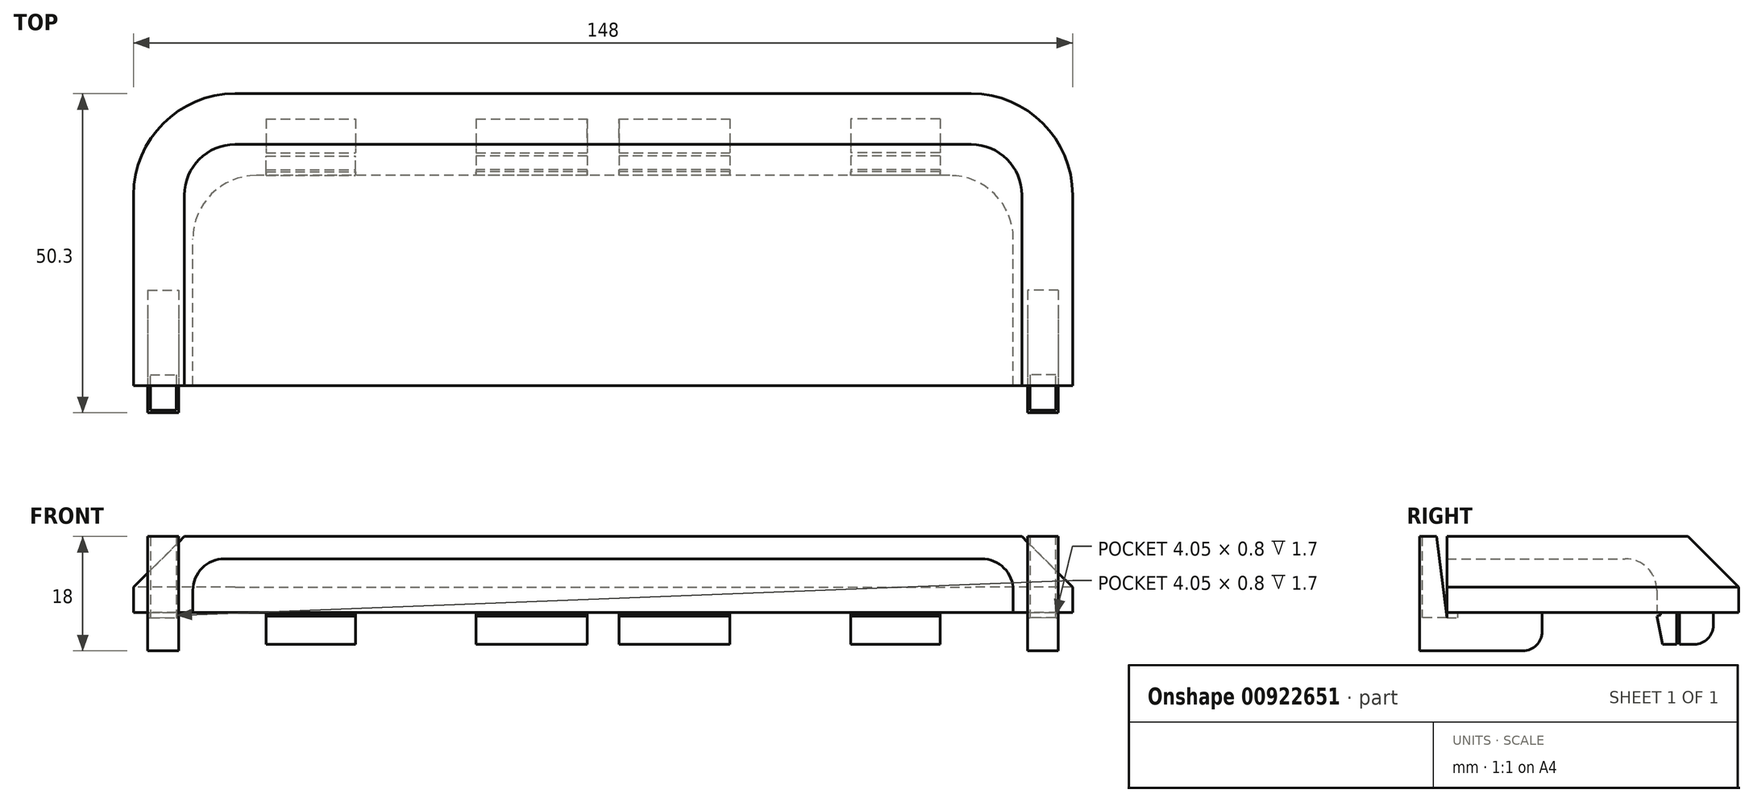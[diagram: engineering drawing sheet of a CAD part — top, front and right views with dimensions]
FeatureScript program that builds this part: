
annotation { "Feature Type Name" : "Feature", "Feature Type Description" : "" }
export const myFeature = defineFeature(function(context is Context, id is Id, definition is map)
    precondition{}
    {
        {
            var Q0;
            Q0=qCreatedBy(makeId("Top.planeOp"),FACE);
            var sketch = newSketch(context, id + "F0", { "sketchPlane" : qUnion([Q0])});
            skLineSegment(sketch, "E0.bottom", {"start": v(-20, 0) * mm, "end": v(20, 0) * mm});
            skLineSegment(sketch, "E0.top", {"start": v(-20, -8.3) * mm, "end": v(20, -8.3) * mm});
            skLineSegment(sketch, "E0.left", {"start": v(-20, 0) * mm, "end": v(-20, -8.3) * mm});
            skLineSegment(sketch, "E0.right", {"start": v(20, 0) * mm, "end": v(20, -8.3) * mm});
            skLineSegment(sketch, "E1.bottom", {"start": v(-53.1, 0) * mm, "end": v(-39, 0) * mm});
            skLineSegment(sketch, "E1.top", {"start": v(-53.1, -8.3) * mm, "end": v(-39, -8.3) * mm});
            skLineSegment(sketch, "E1.left", {"start": v(-53.1, 0) * mm, "end": v(-53.1, -8.3) * mm});
            skLineSegment(sketch, "E1.right", {"start": v(-39, 0) * mm, "end": v(-39, -8.3) * mm});
            skLineSegment(sketch, "E2.MirrorCS", {"start": v(53.1, -8.3) * mm, "end": v(39, -8.3) * mm});
            skLineSegment(sketch, "E3.MirrorCS", {"start": v(39, 0) * mm, "end": v(39, -8.3) * mm});
            skLineSegment(sketch, "E4.MirrorCS", {"start": v(53.1, 0) * mm, "end": v(39, 0) * mm});
            skLineSegment(sketch, "E5.MirrorCS", {"start": v(53.1, 0) * mm, "end": v(53.1, -8.3) * mm});
            skLineSegment(sketch, "E6.bottom", {"start": v(-71.75, -27) * mm, "end": v(-66.9, -27) * mm});
            skLineSegment(sketch, "E6.top", {"start": v(-71.75, -40.3) * mm, "end": v(-66.9, -40.3) * mm});
            skLineSegment(sketch, "E6.left", {"start": v(-71.75, -27) * mm, "end": v(-71.75, -40.3) * mm});
            skLineSegment(sketch, "E6.right", {"start": v(-66.9, -27) * mm, "end": v(-66.9, -40.3) * mm});
            skLineSegment(sketch, "E7.MirrorCS", {"start": v(71.75, -27) * mm, "end": v(66.9, -27) * mm});
            skLineSegment(sketch, "E8.MirrorCS", {"start": v(71.75, -27) * mm, "end": v(71.75, -40.3) * mm});
            skLineSegment(sketch, "E9.MirrorCS", {"start": v(71.75, -40.3) * mm, "end": v(66.9, -40.3) * mm});
            skLineSegment(sketch, "E10.MirrorCS", {"start": v(66.9, -27) * mm, "end": v(66.9, -40.3) * mm});
            skLineSegment(sketch, "E11.bottom", {"start": v(-75, 10.7) * mm, "end": v(75, 10.7) * mm});
            skLineSegment(sketch, "E11.top", {"start": v(-75, -54.3) * mm, "end": v(75, -54.3) * mm});
            skLineSegment(sketch, "E11.left", {"start": v(-75, 10.7) * mm, "end": v(-75, -54.3) * mm});
            skLineSegment(sketch, "E11.right", {"start": v(75, 10.7) * mm, "end": v(75, -54.3) * mm});
            skSolve(sketch);
        }
        {
            var Q0;
            Q0=qCreatedBy(makeId("Top.planeOp"),FACE);
            var sketch = newSketch(context, id + "F1", { "sketchPlane" : qUnion([Q0])});
            skLineSegment(sketch, "E12.bottom", {"start": v(-58, 4) * mm, "end": v(58, 4) * mm});
            skLineSegment(sketch, "E12.top", {"start": v(-74, -42) * mm, "end": v(74, -42) * mm});
            skLineSegment(sketch, "E12.left", {"start": v(-74, -12) * mm, "end": v(-74, -42) * mm});
            skLineSegment(sketch, "E12.right", {"start": v(74, -12) * mm, "end": v(74, -42) * mm});
            skPoint(sketch, "E13.visualSharp", {"position": v(74, 4) * mm});
            skArc(sketch, "E13.filletArc", {"start": v(74, -12) * mm, "mid": v(69.31, -0.69) * mm, "end": v(58, 4) * mm});
            skPoint(sketch, "E14.visualSharp", {"position": v(-74, 4) * mm});
            skArc(sketch, "E14.filletArc", {"start": v(-58, 4) * mm, "mid": v(-69.31, -0.69) * mm, "end": v(-74, -12) * mm});
            skSolve(sketch);
        }
        {
            var Q0;
            Q0 = qSketchRegion(id + "F1", true);
            extrude(context, id + "F2", {"entities" : qUnion([Q0]), "depth" : 12 * mm, "offsetDistance" : 25 * mm});
        }
        {
            var Q0;
            Q0=makeQuery(id+"F2.opExtrude","CAP_EDGE",EDGE,{"disambiguationData":[OSD([sQuery(id+"F1.wireOp",EDGE,"E12.right")])],"isStart":false});
            var Q1;
            Q1=makeQuery(id+"F2.opExtrude","CAP_EDGE",EDGE,{"disambiguationData":[OSD([sQuery(id+"F1.wireOp",EDGE,"E12.bottom")])],"isStart":false});
            var Q2;
            Q2=makeQuery(id+"F2.opExtrude","CAP_EDGE",EDGE,{"disambiguationData":[OSD([sQuery(id+"F1.wireOp",EDGE,"E12.left")])],"isStart":false});
            chamfer(context, id + "F3", {"entities" : qUnion([Q0, Q1, Q2]), "width" : 8 * mm, "tangentPropagation" : true});
        }
        {
            var Q0;
            Q0=makeQuery(id+"F0.imprint","IMPRINT",FACE,{"disambiguationData":[TD([[makeQuery(id+"F0.imprint","IMPRINT",EDGE,{"derivedFrom":sQuery(id+"F0.wireOp",EDGE,"E1.bottom")}),-1.0]])]});
            var Q1;
            Q1=makeQuery(id+"F0.imprint","IMPRINT",FACE,{"disambiguationData":[TD([[makeQuery(id+"F0.imprint","IMPRINT",EDGE,{"derivedFrom":sQuery(id+"F0.wireOp",EDGE,"E0.bottom")}),-1.0]])]});
            var Q2;
            Q2=makeQuery(id+"F0.imprint","IMPRINT",FACE,{"disambiguationData":[TD([[makeQuery(id+"F0.imprint","IMPRINT",EDGE,{"derivedFrom":sQuery(id+"F0.wireOp",EDGE,"E2.MirrorCS")}),-1.0]])]});
            extrude(context, id + "F4", {"entities" : qUnion([Q0, Q1, Q2]), "operationType" : NewBodyOperationType.ADD, "oppositeDirection" : true, "depth" : 5 * mm, "offsetDistance" : 25 * mm});
        }
        {
            var Q0;
            Q0=qCreatedBy(makeId("Right.planeOp"),FACE);
            var sketch = newSketch(context, id + "F5", { "sketchPlane" : qUnion([Q0])});
            skLineSegment(sketch, "E15", {"start": v(-8.3, 0) * mm, "end": v(-8.3, -0.35) * mm});
            skLineSegment(sketch, "E16", {"start": v(-8.3, -0.35) * mm, "end": v(-8.9, -0.55) * mm});
            skLineSegment(sketch, "E17", {"start": v(-8.9, -0.55) * mm, "end": v(-8, -5) * mm});
            skLineSegment(sketch, "E18", {"start": v(-8, -5) * mm, "end": v(-5.8, -5) * mm});
            skLineSegment(sketch, "E19", {"start": v(-5.8, -5) * mm, "end": v(-5.8, 0) * mm});
            skLineSegment(sketch, "E20", {"start": v(-8.3, 0) * mm, "end": v(-5.8, 0) * mm});
            skSolve(sketch);
        }
        {
            var Q0;
            Q0=makeQuery(id+"F4.opExtrude","SWEPT_FACE",FACE,{"disambiguationData":[OSD([sQuery(id+"F0.wireOp",EDGE,"E0.top")])]});
            var Q1;
            Q1=makeQuery(id+"F4.opExtrude","SWEPT_FACE",FACE,{"disambiguationData":[OSD([sQuery(id+"F0.wireOp",EDGE,"E2.MirrorCS")])]});
            var Q2;
            Q2=makeQuery(id+"F4.opExtrude","SWEPT_FACE",FACE,{"disambiguationData":[OSD([sQuery(id+"F0.wireOp",EDGE,"E1.top")])]});
            extrude(context, id + "F6", {"entities" : qUnion([Q0, Q1, Q2]), "operationType" : NewBodyOperationType.REMOVE, "oppositeDirection" : true, "depth" : 3 * mm, "offsetDistance" : 25 * mm});
        }
        {
            var Q0;
            Q0 = qSketchRegion(id + "F5", true);
            var Q1;
            Q1=makeQuery(id+"F4.opExtrude","SWEPT_FACE",FACE,{"disambiguationData":[OSD([sQuery(id+"F0.wireOp",EDGE,"E0.right")])]});
            var Q2;
            Q2=makeQuery(id+"F4.opExtrude","SWEPT_FACE",FACE,{"disambiguationData":[OSD([sQuery(id+"F0.wireOp",EDGE,"E0.left")])]});
            extrude(context, id + "F7", {"entities" : qUnion([Q0]), "operationType" : NewBodyOperationType.ADD, "endBound" : BoundingType.UP_TO_SURFACE, "depth" : 25 * mm, "endBoundEntityFace" : qUnion([Q1]), "offsetDistance" : 25 * mm, "hasSecondDirection" : true, "secondDirectionBound" : BoundingType.UP_TO_SURFACE, "secondDirectionOppositeDirection" : true, "secondDirectionDepth" : 25 * mm, "secondDirectionBoundEntityFace" : qUnion([Q2])});
        }
        {
            var Q0;
            Q0 = qSketchRegion(id + "F5", true);
            var Q1;
            Q1=makeQuery(id+"F4.opExtrude","SWEPT_FACE",FACE,{"disambiguationData":[OSD([sQuery(id+"F0.wireOp",EDGE,"E5.MirrorCS")])]});
            var Q2;
            Q2=makeQuery(id+"F4.opExtrude","SWEPT_FACE",FACE,{"disambiguationData":[OSD([sQuery(id+"F0.wireOp",EDGE,"E3.MirrorCS")])]});
            extrude(context, id + "F8", {"entities" : qUnion([Q0]), "operationType" : NewBodyOperationType.ADD, "endBound" : BoundingType.UP_TO_SURFACE, "depth" : 25 * mm, "endBoundEntityFace" : qUnion([Q1]), "offsetDistance" : 25 * mm, "hasSecondDirection" : true, "secondDirectionBound" : BoundingType.UP_TO_SURFACE, "secondDirectionOppositeDirection" : false, "secondDirectionDepth" : 25 * mm, "secondDirectionBoundEntityFace" : qUnion([Q2])});
        }
        {
            var Q0;
            Q0 = qSketchRegion(id + "F5", true);
            var Q1;
            Q1=makeQuery(id+"F4.opExtrude","SWEPT_FACE",FACE,{"disambiguationData":[OSD([sQuery(id+"F0.wireOp",EDGE,"E1.left")])]});
            var Q2;
            Q2=makeQuery(id+"F4.opExtrude","SWEPT_FACE",FACE,{"disambiguationData":[OSD([sQuery(id+"F0.wireOp",EDGE,"E1.right")])]});
            extrude(context, id + "F9", {"entities" : qUnion([Q0]), "operationType" : NewBodyOperationType.ADD, "endBound" : BoundingType.UP_TO_SURFACE, "oppositeDirection" : true, "depth" : 25 * mm, "endBoundEntityFace" : qUnion([Q1]), "offsetDistance" : 25 * mm, "hasSecondDirection" : true, "secondDirectionBound" : BoundingType.UP_TO_SURFACE, "secondDirectionOppositeDirection" : true, "secondDirectionDepth" : 25 * mm, "secondDirectionBoundEntityFace" : qUnion([Q2])});
        }
        {
            var Q0;
            Q0=makeQuery(id+"F0.imprint","IMPRINT",FACE,{"disambiguationData":[TD([[makeQuery(id+"F0.imprint","IMPRINT",EDGE,{"derivedFrom":sQuery(id+"F0.wireOp",EDGE,"E7.MirrorCS")}),1.0]])]});
            var Q1;
            Q1=makeQuery(id+"F0.imprint","IMPRINT",FACE,{"disambiguationData":[TD([[makeQuery(id+"F0.imprint","IMPRINT",EDGE,{"derivedFrom":sQuery(id+"F0.wireOp",EDGE,"E6.bottom")}),-1.0]])]});
            extrude(context, id + "F10", {"entities" : qUnion([Q0, Q1]), "operationType" : NewBodyOperationType.ADD, "oppositeDirection" : true, "depth" : 6 * mm, "offsetDistance" : 25 * mm});
        }
        {
            var Q0;
            Q0=makeQuery(id+"F2.opExtrude","CAP_FACE",FACE,{"disambiguationData":[OSD([sQuery(id+"F1.wireOp",EDGE,"E12.bottom"),sQuery(id+"F1.wireOp",EDGE,"E12.top"),sQuery(id+"F1.wireOp",EDGE,"E12.left"),sQuery(id+"F1.wireOp",EDGE,"E12.right"),sQuery(id+"F1.wireOp",EDGE,"E13.filletArc"),sQuery(id+"F1.wireOp",EDGE,"E14.filletArc")])],"isStart":true});
            var sketch = newSketch(context, id + "F11", { "sketchPlane" : qUnion([Q0])});
            skLineSegment(sketch, "E21.bottom", {"start": v(64.65, 42) * mm, "end": v(-64.65, 42) * mm});
            skLineSegment(sketch, "E21.top", {"start": v(54.65, 8.9) * mm, "end": v(-54.65, 8.9) * mm});
            skLineSegment(sketch, "E21.left", {"start": v(64.65, 42) * mm, "end": v(64.65, 18.9) * mm});
            skLineSegment(sketch, "E21.right", {"start": v(-64.65, 42) * mm, "end": v(-64.65, 18.9) * mm});
            skLineSegment(sketch, "E22.0", {"start": v(66, 42) * mm, "end": v(66, 12) * mm, "construction": true});
            skLineSegment(sketch, "E23.0", {"start": v(58, 4) * mm, "end": v(-58, 4) * mm, "construction": true});
            skPoint(sketch, "E24.visualSharp", {"position": v(64.65, 8.9) * mm});
            skArc(sketch, "E24.filletArc", {"start": v(54.65, 8.9) * mm, "mid": v(61.72, 11.83) * mm, "end": v(64.65, 18.9) * mm});
            skPoint(sketch, "E25.visualSharp", {"position": v(-64.65, 8.9) * mm});
            skArc(sketch, "E25.filletArc", {"start": v(-64.65, 18.9) * mm, "mid": v(-61.72, 11.83) * mm, "end": v(-54.65, 8.9) * mm});
            skSolve(sketch);
        }
        {
            var Q0;
            Q0 = qSketchRegion(id + "F11", true);
            extrude(context, id + "F12", {"entities" : qUnion([Q0]), "operationType" : NewBodyOperationType.REMOVE, "oppositeDirection" : true, "depth" : 8.5 * mm, "offsetDistance" : 25 * mm});
        }
        {
            var Q0;
            Q0=makeQuery(id+"F10.opExtrude","SWEPT_FACE",FACE,{"disambiguationData":[OSD([sQuery(id+"F0.wireOp",EDGE,"E9.MirrorCS")])]});
            var sketch = newSketch(context, id + "F13", { "sketchPlane" : qUnion([Q0])});
            skLineSegment(sketch, "E26.bottom", {"start": v(71.75, -6) * mm, "end": v(66.9, -6) * mm});
            skLineSegment(sketch, "E26.top", {"start": v(71.75, -0.8) * mm, "end": v(66.9, -0.8) * mm});
            skLineSegment(sketch, "E26.left", {"start": v(71.75, -6) * mm, "end": v(71.75, -0.8) * mm});
            skLineSegment(sketch, "E26.right", {"start": v(66.9, -6) * mm, "end": v(66.9, -0.8) * mm});
            skLineSegment(sketch, "E27.MirrorCS", {"start": v(-71.75, -6) * mm, "end": v(-66.9, -6) * mm});
            skLineSegment(sketch, "E28.MirrorCS", {"start": v(-71.75, -6) * mm, "end": v(-71.75, -0.8) * mm});
            skLineSegment(sketch, "E29.MirrorCS", {"start": v(-71.75, -0.8) * mm, "end": v(-66.9, -0.8) * mm});
            skLineSegment(sketch, "E30.MirrorCS", {"start": v(-66.9, -6) * mm, "end": v(-66.9, -0.8) * mm});
            skSolve(sketch);
        }
        {
            var Q0;
            Q0=makeQuery(id+"F13.imprint","IMPRINT",FACE,{"disambiguationData":[TD([[makeQuery(id+"F13.imprint","IMPRINT",EDGE,{"derivedFrom":sQuery(id+"F13.wireOp",EDGE,"E26.bottom")}),-1.0]])]});
            var Q1;
            Q1=makeQuery(id+"F13.imprint","IMPRINT",FACE,{"disambiguationData":[TD([[makeQuery(id+"F13.imprint","IMPRINT",EDGE,{"derivedFrom":sQuery(id+"F13.wireOp",EDGE,"E27.MirrorCS")}),1.0]])]});
            extrude(context, id + "F14", {"entities" : qUnion([Q0, Q1]), "operationType" : NewBodyOperationType.ADD, "depth" : 6 * mm, "offsetDistance" : 25 * mm});
        }
        {
            var Q0;
            Q0=makeQuery(id+"F4.opExtrude","CAP_EDGE",EDGE,{"disambiguationData":[OSD([sQuery(id+"F0.wireOp",EDGE,"E0.bottom")])],"isStart":false});
            var Q1;
            Q1=makeQuery(id+"F4.opExtrude","CAP_EDGE",EDGE,{"disambiguationData":[OSD([sQuery(id+"F0.wireOp",EDGE,"E1.bottom")])],"isStart":false});
            var Q2;
            Q2=makeQuery(id+"F4.opExtrude","CAP_EDGE",EDGE,{"disambiguationData":[OSD([sQuery(id+"F0.wireOp",EDGE,"E4.MirrorCS")])],"isStart":false});
            var Q3;
            Q3=makeQuery(id+"F10.opExtrude","CAP_EDGE",EDGE,{"disambiguationData":[OSD([sQuery(id+"F0.wireOp",EDGE,"E6.bottom")])],"isStart":false});
            var Q4;
            Q4=makeQuery(id+"F10.opExtrude","CAP_EDGE",EDGE,{"disambiguationData":[OSD([sQuery(id+"F0.wireOp",EDGE,"E7.MirrorCS")])],"isStart":false});
            var Q5;
            Q5=makeQuery(id+"F10.opExtrude","CAP_EDGE",EDGE,{"disambiguationData":[OSD([sQuery(id+"F0.wireOp",EDGE,"E7.MirrorCS")])],"isStart":true});
            var Q6;
            Q6=makeQuery(id+"F10.opExtrude","CAP_EDGE",EDGE,{"disambiguationData":[OSD([sQuery(id+"F0.wireOp",EDGE,"E6.bottom")])],"isStart":true});
            fillet(context, id + "F15", {"entities" : qUnion([Q0, Q1, Q2, Q3, Q4, Q5, Q6]), "radius" : 3 * mm, "tangentPropagation" : true, "allowEdgeOverflow" : false});
        }
        {
            var Q0;
            Q0=makeQuery(id+"F12.boolean.opBoolean","COPY",EDGE,{"derivedFrom":makeQuery(id+"F12.opExtrude","CAP_EDGE",EDGE,{"disambiguationData":[OSD([sQuery(id+"F11.wireOp",EDGE,"E21.left")])],"isStart":false})});
            fillet(context, id + "F16", {"entities" : qUnion([Q0]), "radius" : 5 * mm, "tangentPropagation" : true, "allowEdgeOverflow" : false});
        }
        {
            var Q0;
            Q0=makeQuery(id+"F4.opExtrude","CAP_FACE",FACE,{"disambiguationData":[OSD([sQuery(id+"F0.wireOp",EDGE,"E0.bottom"),sQuery(id+"F0.wireOp",EDGE,"E0.top"),sQuery(id+"F0.wireOp",EDGE,"E0.left"),sQuery(id+"F0.wireOp",EDGE,"E0.right")])],"isStart":false});
            var sketch = newSketch(context, id + "F17", { "sketchPlane" : qUnion([Q0])});
            skLineSegment(sketch, "E31.bottom", {"start": v(2.5, 0) * mm, "end": v(-2.5, 0) * mm});
            skLineSegment(sketch, "E31.top", {"start": v(2.5, 8.9) * mm, "end": v(-2.5, 8.9) * mm});
            skLineSegment(sketch, "E31.left", {"start": v(2.5, 0) * mm, "end": v(2.5, 8.9) * mm});
            skLineSegment(sketch, "E31.right", {"start": v(-2.5, 0) * mm, "end": v(-2.5, 8.9) * mm});
            skSolve(sketch);
        }
        {
            var Q0;
            Q0 = qSketchRegion(id + "F17", true);
            var Q1;
            {var subQ0=sQuery(id+"F0.wireOp",EDGE,"E2.MirrorCS");var subQ1=sQuery(id+"F0.wireOp",EDGE,"E1.top");var subQ2=sQuery(id+"F0.wireOp",EDGE,"E0.top");Q1=makeQuery(id+"F6.boolean.opBoolean","MERGE",FACE,{"derivedFrom":[makeQuery(id+"F2.opExtrude","CAP_FACE",FACE,{"disambiguationData":[OSD([sQuery(id+"F1.wireOp",EDGE,"E12.bottom"),sQuery(id+"F1.wireOp",EDGE,"E12.top"),sQuery(id+"F1.wireOp",EDGE,"E12.left"),sQuery(id+"F1.wireOp",EDGE,"E12.right"),sQuery(id+"F1.wireOp",EDGE,"E13.filletArc"),sQuery(id+"F1.wireOp",EDGE,"E14.filletArc")])],"isStart":true})],"fromTools":[makeQuery(id+"F6.opExtrude","SWEPT_FACE",FACE,{"disambiguationData":[OSD([subQ2]),TDD([makeQuery(id+"F4.opExtrude","CAP_EDGE",EDGE,{"disambiguationData":[OSD([subQ2])],"isStart":true})])]}),makeQuery(id+"F6.opExtrude","SWEPT_FACE",FACE,{"disambiguationData":[OSD([subQ1]),TDD([makeQuery(id+"F4.opExtrude","CAP_EDGE",EDGE,{"disambiguationData":[OSD([subQ1])],"isStart":true})])]}),makeQuery(id+"F6.opExtrude","SWEPT_FACE",FACE,{"disambiguationData":[OSD([subQ0]),TDD([makeQuery(id+"F4.opExtrude","CAP_EDGE",EDGE,{"disambiguationData":[OSD([subQ0])],"isStart":true})])]})]});}
            extrude(context, id + "F18", {"entities" : qUnion([Q0]), "operationType" : NewBodyOperationType.REMOVE, "endBound" : BoundingType.UP_TO_SURFACE, "oppositeDirection" : true, "depth" : 25 * mm, "endBoundEntityFace" : qUnion([Q1]), "offsetDistance" : 25 * mm});
        }
        {
            var Q0;
            Q0=makeQuery(id+"F14.opExtrude","SWEPT_FACE",FACE,{"disambiguationData":[OSD([sQuery(id+"F13.wireOp",EDGE,"E26.top")])]});
            var sketch = newSketch(context, id + "F19", { "sketchPlane" : qUnion([Q0])});
            skLineSegment(sketch, "E32.0.0", {"start": v(71.75, -40.3) * mm, "end": v(71.35, -40.3) * mm});
            skLineSegment(sketch, "E32.0.1", {"start": v(66.9, -40.3) * mm, "end": v(66.9, -46.3) * mm});
            skLineSegment(sketch, "E32.0.2", {"start": v(66.9, -46.3) * mm, "end": v(71.75, -46.3) * mm});
            skLineSegment(sketch, "E32.0.3", {"start": v(71.75, -46.3) * mm, "end": v(71.75, -40.3) * mm});
            skLineSegment(sketch, "E33.1", {"start": v(71.35, -45.9) * mm, "end": v(71.35, -40.3) * mm});
            skLineSegment(sketch, "E33.2", {"start": v(67.3, -45.9) * mm, "end": v(71.35, -45.9) * mm});
            skLineSegment(sketch, "E33.3", {"start": v(67.3, -40.3) * mm, "end": v(67.3, -45.9) * mm});
            skLineSegment(sketch, "E34.trimOffspring", {"start": v(67.3, -40.3) * mm, "end": v(66.9, -40.3) * mm});
            skLineSegment(sketch, "E35.MirrorCS", {"start": v(-71.75, -40.3) * mm, "end": v(-71.35, -40.3) * mm});
            skLineSegment(sketch, "E36.MirrorCS", {"start": v(-67.3, -45.9) * mm, "end": v(-71.35, -45.9) * mm});
            skLineSegment(sketch, "E37.MirrorCS", {"start": v(-66.9, -46.3) * mm, "end": v(-71.75, -46.3) * mm});
            skLineSegment(sketch, "E38.MirrorCS", {"start": v(-67.3, -40.3) * mm, "end": v(-66.9, -40.3) * mm});
            skLineSegment(sketch, "E39.MirrorCS", {"start": v(-67.3, -40.3) * mm, "end": v(-67.3, -45.9) * mm});
            skLineSegment(sketch, "E40.MirrorCS", {"start": v(-71.35, -45.9) * mm, "end": v(-71.35, -40.3) * mm});
            skLineSegment(sketch, "E41.MirrorCS", {"start": v(-66.9, -40.3) * mm, "end": v(-66.9, -46.3) * mm});
            skLineSegment(sketch, "E42.MirrorCS", {"start": v(-71.75, -46.3) * mm, "end": v(-71.75, -40.3) * mm});
            skSolve(sketch);
        }
        {
            var Q0;
            Q0 = qSketchRegion(id + "F19", true);
            var Q1;
            {var subQ0=sQuery(id+"F0.wireOp",EDGE,"E2.MirrorCS");var subQ1=sQuery(id+"F0.wireOp",EDGE,"E1.top");var subQ2=sQuery(id+"F0.wireOp",EDGE,"E0.top");Q1=makeQuery(id+"F18.boolean.opBoolean","MERGE",FACE,{"derivedFrom":[makeQuery(id+"F6.boolean.opBoolean","MERGE",FACE,{"derivedFrom":[makeQuery(id+"F2.opExtrude","CAP_FACE",FACE,{"disambiguationData":[OSD([sQuery(id+"F1.wireOp",EDGE,"E12.bottom"),sQuery(id+"F1.wireOp",EDGE,"E12.top"),sQuery(id+"F1.wireOp",EDGE,"E12.left"),sQuery(id+"F1.wireOp",EDGE,"E12.right"),sQuery(id+"F1.wireOp",EDGE,"E13.filletArc"),sQuery(id+"F1.wireOp",EDGE,"E14.filletArc")])],"isStart":true})],"fromTools":[makeQuery(id+"F6.opExtrude","SWEPT_FACE",FACE,{"disambiguationData":[OSD([subQ2]),TDD([makeQuery(id+"F4.opExtrude","CAP_EDGE",EDGE,{"disambiguationData":[OSD([subQ2])],"isStart":true})])]}),makeQuery(id+"F6.opExtrude","SWEPT_FACE",FACE,{"disambiguationData":[OSD([subQ1]),TDD([makeQuery(id+"F4.opExtrude","CAP_EDGE",EDGE,{"disambiguationData":[OSD([subQ1])],"isStart":true})])]}),makeQuery(id+"F6.opExtrude","SWEPT_FACE",FACE,{"disambiguationData":[OSD([subQ0]),TDD([makeQuery(id+"F4.opExtrude","CAP_EDGE",EDGE,{"disambiguationData":[OSD([subQ0])],"isStart":true})])]})]})],"fromTools":[makeQuery(id+"F18.opExtrude","CAP_FACE",FACE,{"disambiguationData":[OSD([sQuery(id+"F17.wireOp",EDGE,"E31.bottom"),sQuery(id+"F17.wireOp",EDGE,"E31.top"),sQuery(id+"F17.wireOp",EDGE,"E31.left"),sQuery(id+"F17.wireOp",EDGE,"E31.right")])],"isStart":false})]});}
            extrude(context, id + "F20", {"entities" : qUnion([Q0]), "operationType" : NewBodyOperationType.ADD, "endBound" : BoundingType.UP_TO_SURFACE, "depth" : 25 * mm, "endBoundEntityFace" : qUnion([Q1]), "offsetDistance" : 25 * mm});
        }
        {
            var Q0;
            Q0=makeQuery(id+"F20.opExtrude","CAP_FACE",FACE,{"disambiguationData":[OSD([sQuery(id+"F19.wireOp",EDGE,"E32.0.0"),sQuery(id+"F19.wireOp",EDGE,"E32.0.1"),sQuery(id+"F19.wireOp",EDGE,"E32.0.2"),sQuery(id+"F19.wireOp",EDGE,"E32.0.3"),sQuery(id+"F19.wireOp",EDGE,"E33.1"),sQuery(id+"F19.wireOp",EDGE,"E33.2"),sQuery(id+"F19.wireOp",EDGE,"E33.3"),sQuery(id+"F19.wireOp",EDGE,"E34.trimOffspring")])],"isStart":false});
            var Q1;
            Q1=makeQuery(id+"F20.opExtrude","CAP_FACE",FACE,{"disambiguationData":[OSD([sQuery(id+"F19.wireOp",EDGE,"E35.MirrorCS"),sQuery(id+"F19.wireOp",EDGE,"E36.MirrorCS"),sQuery(id+"F19.wireOp",EDGE,"E37.MirrorCS"),sQuery(id+"F19.wireOp",EDGE,"E38.MirrorCS"),sQuery(id+"F19.wireOp",EDGE,"E39.MirrorCS"),sQuery(id+"F19.wireOp",EDGE,"E40.MirrorCS"),sQuery(id+"F19.wireOp",EDGE,"E41.MirrorCS"),sQuery(id+"F19.wireOp",EDGE,"E42.MirrorCS")])],"isStart":false});
            var Q2;
            Q2=makeQuery(id+"F2.opExtrude","CAP_FACE",FACE,{"disambiguationData":[OSD([sQuery(id+"F1.wireOp",EDGE,"E12.bottom"),sQuery(id+"F1.wireOp",EDGE,"E12.top"),sQuery(id+"F1.wireOp",EDGE,"E12.left"),sQuery(id+"F1.wireOp",EDGE,"E12.right"),sQuery(id+"F1.wireOp",EDGE,"E13.filletArc"),sQuery(id+"F1.wireOp",EDGE,"E14.filletArc")])],"isStart":false});
            extrude(context, id + "F21", {"entities" : qUnion([Q0, Q1]), "operationType" : NewBodyOperationType.ADD, "endBound" : BoundingType.UP_TO_SURFACE, "depth" : 25 * mm, "endBoundEntityFace" : qUnion([Q2]), "offsetDistance" : 25 * mm});
        }
        {
            var Q0;
            {var subQ0=sQuery(id+"F19.wireOp",EDGE,"E32.0.3");Q0=makeQuery(id+"F21.boolean.opBoolean","MERGE",FACE,{"derivedFrom":[makeQuery(id+"F20.boolean.opBoolean","MERGE",FACE,{"derivedFrom":[makeQuery(id+"F14.boolean.opBoolean","MERGE",FACE,{"derivedFrom":[makeQuery(id+"F10.opExtrude","SWEPT_FACE",FACE,{"disambiguationData":[OSD([sQuery(id+"F0.wireOp",EDGE,"E8.MirrorCS")])]}),makeQuery(id+"F14.opExtrude","SWEPT_FACE",FACE,{"disambiguationData":[OSD([sQuery(id+"F13.wireOp",EDGE,"E26.left")])]})]}),makeQuery(id+"F20.opExtrude","SWEPT_FACE",FACE,{"disambiguationData":[OSD([subQ0])]})]}),makeQuery(id+"F21.opExtrude","SWEPT_FACE",FACE,{"disambiguationData":[OSD([subQ0])]})]});}
            var sketch = newSketch(context, id + "F22", { "sketchPlane" : qUnion([Q0])});
            skLineSegment(sketch, "E43.0", {"start": v(-42, 12) * mm, "end": v(-42, -0.8) * mm});
            skLineSegment(sketch, "E44.0", {"start": v(-46.3, 12) * mm, "end": v(-42, 12) * mm});
            skLineSegment(sketch, "E45", {"start": v(-43.65, 12) * mm, "end": v(-42, -0.8) * mm});
            skPoint(sketch, "E46.orphan", {"position": v(-42, 6.25) * mm});
            skSolve(sketch);
        }
        {
            var Q0;
            Q0 = qSketchRegion(id + "F22", true);
            extrude(context, id + "F23", {"entities" : qUnion([Q0]), "operationType" : NewBodyOperationType.REMOVE, "endBound" : BoundingType.THROUGH_ALL, "oppositeDirection" : true, "depth" : 25 * mm, "offsetDistance" : 25 * mm});
        }
    });
